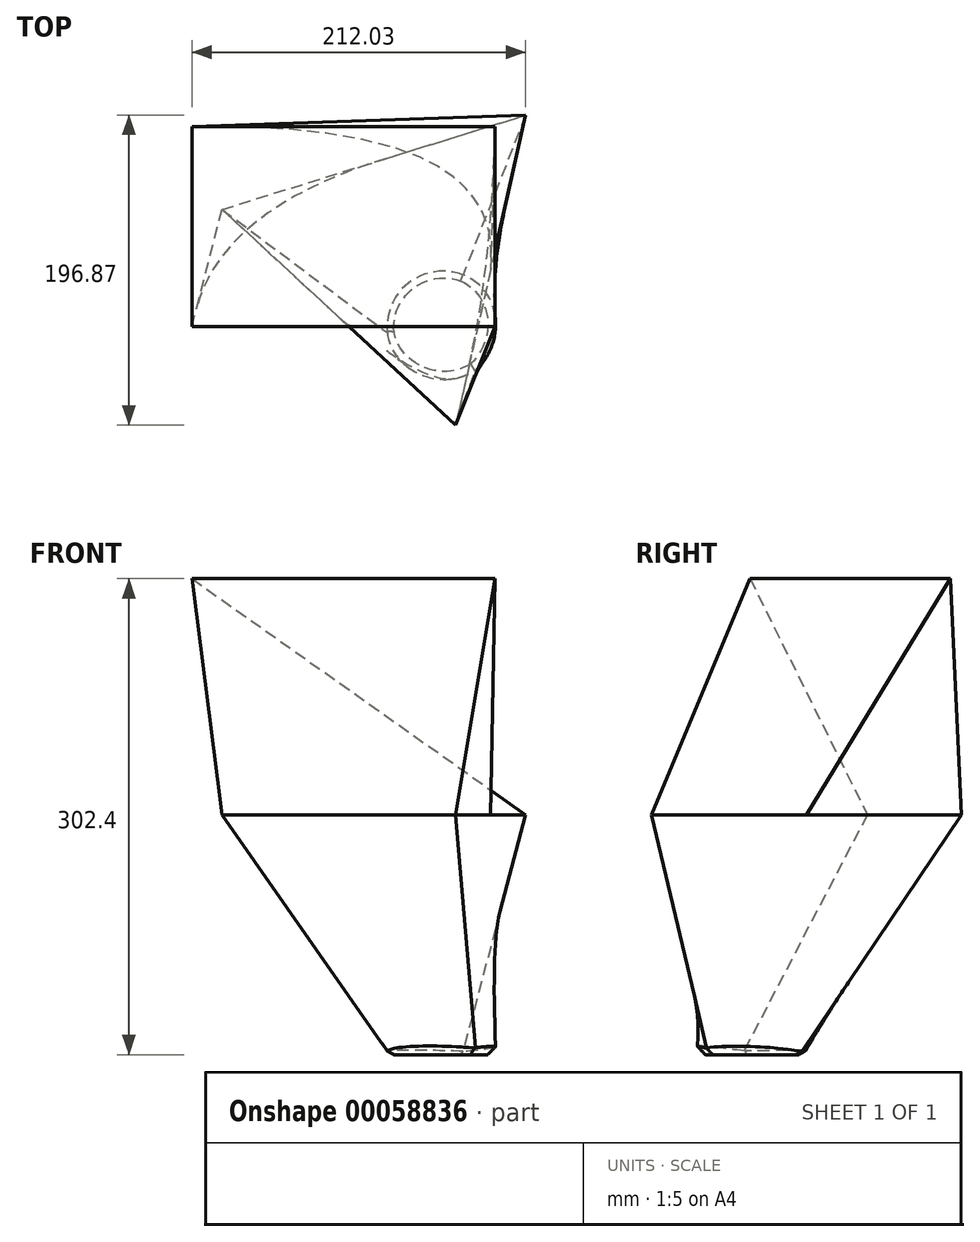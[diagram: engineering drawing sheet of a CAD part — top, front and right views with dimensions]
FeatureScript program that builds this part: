
annotation { "Feature Type Name" : "Feature", "Feature Type Description" : "" }
export const myFeature = defineFeature(function(context is Context, id is Id, definition is map)
    precondition{}
    {
        {
            var Q0;
            Q0=qCreatedBy(makeId("Top.planeOp"),FACE);
            var sketch = newSketch(context, id + "F0", { "sketchPlane" : qUnion([Q0])});
            skCircle(sketch, "E0", {"center": v(0, 0) * mm, "radius": 33.86 * mm});
            skSolve(sketch);
        }
        {
            var Q0;
            Q0=qCreatedBy(makeId("Top.planeOp"),FACE);
            cPlane(context, id + "F1", {"entities" : qUnion([Q0]), "cplaneType" : CPlaneType.OFFSET, "offset" : 152.4 * mm, "width" : 152.4 * mm, "height" : 152.4 * mm});
        }
        {
            var Q0;
            Q0=qCreatedBy(id+"F1.planeOp",FACE);
            var sketch = newSketch(context, id + "F2", { "sketchPlane" : qUnion([Q0])});
            skCircle(sketch, "E1.cCircle", {"center": v(-26.38, 48.84) * mm, "radius": 58.27 * mm, "construction": true});
            skLineSegment(sketch, "E1.0", {"start": v(52.7, 134.42) * mm, "end": v(8.19, -62.45) * mm});
            skLineSegment(sketch, "E1.1", {"start": v(8.19, -62.45) * mm, "end": v(-140.05, 74.54) * mm});
            skLineSegment(sketch, "E1.2", {"start": v(-140.05, 74.54) * mm, "end": v(52.7, 134.42) * mm});
            skPoint(sketch, "E1.0.midPoint", {"position": v(30.45, 35.98) * mm});
            skSolve(sketch);
        }
        {
            var Q0;
            Q0=makeQuery(id+"F2.imprint","IMPRINT",FACE,{"disambiguationData":[TD([[makeQuery(id+"F2.imprint","IMPRINT",EDGE,{"derivedFrom":sQuery(id+"F2.wireOp",EDGE,"E1.0")}),-1.0]])]});
            var Q1;
            Q1=makeQuery(id+"F0.imprint","IMPRINT",FACE,{"disambiguationData":[TD([[makeQuery(id+"F0.imprint","IMPRINT",EDGE,{"derivedFrom":sQuery(id+"F0.wireOp",EDGE,"E0")}),1.0]])]});
            loft(context, id + "F3", {"sheetProfilesArray" : [{ "sheetProfileEntities" : qUnion([Q0]) }, { "sheetProfileEntities" : qUnion([Q1]) }]});
        }
        {
            var Q0;
            Q0=makeQuery(id+"F3.opLoft","CAP_FACE",FACE,{"disambiguationData":[OSD([makeQuery(id+"F0.imprint","IMPRINT",FACE,{"disambiguationData":[TD([[makeQuery(id+"F0.imprint","IMPRINT",EDGE,{"derivedFrom":sQuery(id+"F0.wireOp",EDGE,"E0")}),1.0]])]})])],"isStart":true});
            chamfer(context, id + "F4", {"entities" : qUnion([Q0]), "width" : 5 * mm, "tangentPropagation" : true});
        }
        {
            var Q0;
            Q0=qCreatedBy(id+"F1.planeOp",FACE);
            cPlane(context, id + "F5", {"entities" : qUnion([Q0]), "cplaneType" : CPlaneType.OFFSET, "offset" : 150 * mm, "width" : 150 * mm, "height" : 150 * mm});
        }
        {
            var Q0;
            Q0=qCreatedBy(id+"F5.planeOp",FACE);
            var sketch = newSketch(context, id + "F6", { "sketchPlane" : qUnion([Q0])});
            skLineSegment(sketch, "E2.bottom", {"start": v(-159.32, 0) * mm, "end": v(33.25, 0) * mm});
            skLineSegment(sketch, "E2.top", {"start": v(-159.32, 127.17) * mm, "end": v(33.25, 127.17) * mm});
            skLineSegment(sketch, "E2.left", {"start": v(-159.32, 0) * mm, "end": v(-159.32, 127.17) * mm});
            skLineSegment(sketch, "E2.right", {"start": v(33.25, 0) * mm, "end": v(33.25, 127.17) * mm});
            skSolve(sketch);
        }
        {
            var Q0;
            Q0=makeQuery(id+"F6.imprint","IMPRINT",FACE,{"disambiguationData":[TD([[makeQuery(id+"F6.imprint","IMPRINT",EDGE,{"derivedFrom":sQuery(id+"F6.wireOp",EDGE,"E2.bottom")}),1.0]])]});
            var Q1;
            Q1=makeQuery(id+"F3.opLoft","CAP_FACE",FACE,{"disambiguationData":[OSD([makeQuery(id+"F2.imprint","IMPRINT",FACE,{"disambiguationData":[TD([[makeQuery(id+"F2.imprint","IMPRINT",EDGE,{"derivedFrom":sQuery(id+"F2.wireOp",EDGE,"E1.0")}),-1.0]])]})])],"isStart":true});
            loft(context, id + "F7", {"sheetProfilesArray" : [{ "sheetProfileEntities" : qUnion([Q0]) }, { "sheetProfileEntities" : qUnion([Q1]) }]});
        }
    });
